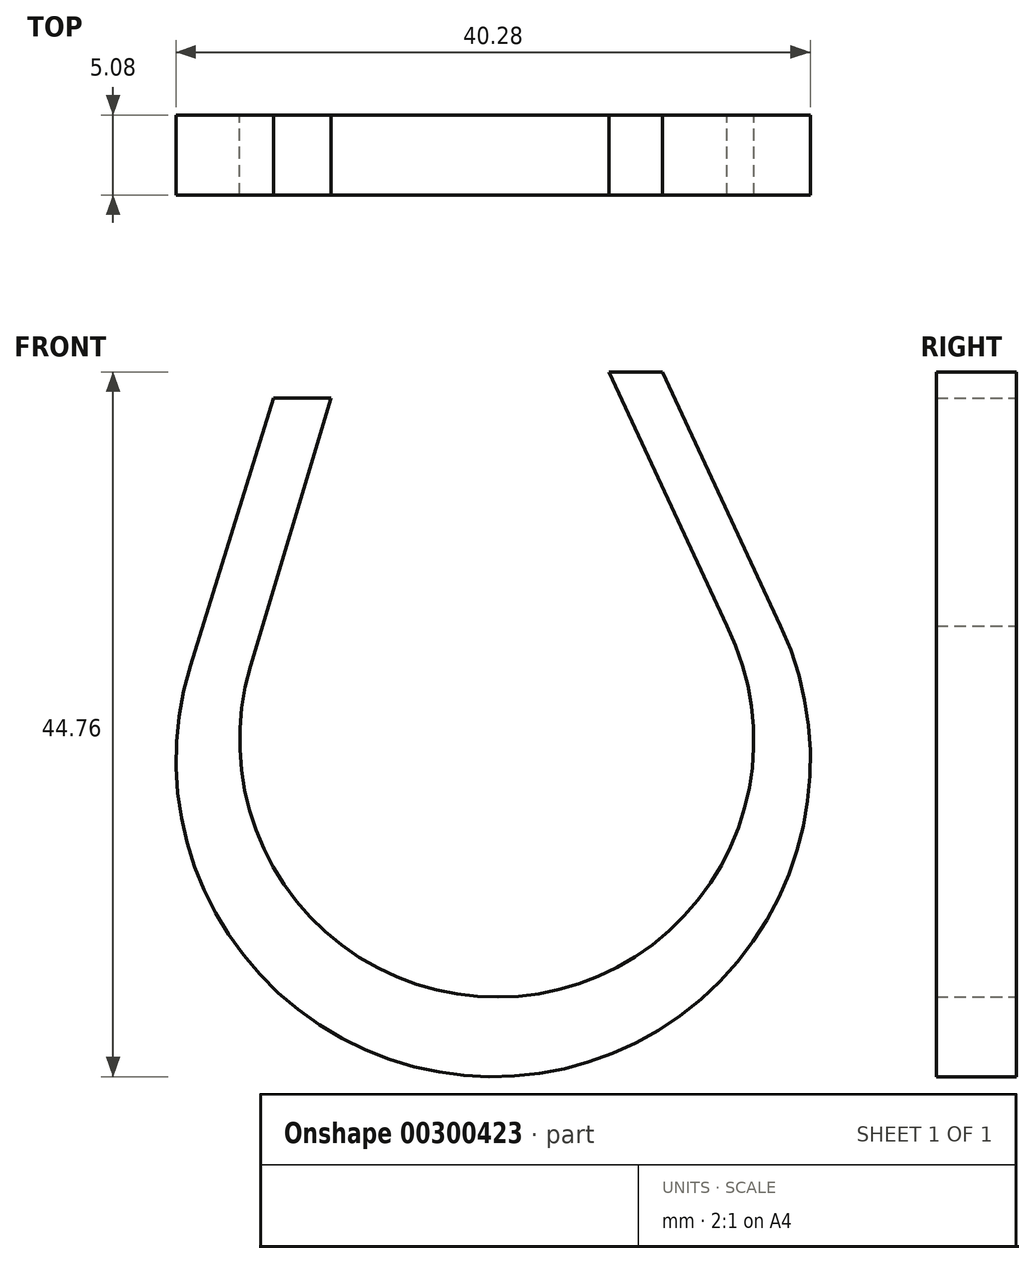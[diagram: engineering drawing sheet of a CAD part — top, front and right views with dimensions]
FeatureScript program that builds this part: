
annotation { "Feature Type Name" : "Feature", "Feature Type Description" : "" }
export const myFeature = defineFeature(function(context is Context, id is Id, definition is map)
    precondition{}
    {
        {
            var Q0;
            Q0=qCreatedBy(makeId("Front.planeOp"),FACE);
            var sketch = newSketch(context, id + "F0", { "sketchPlane" : qUnion([Q0])});
            skArc(sketch, "E0", {"start": v(-30.03, 12.95) * mm, "mid": v(-9.45, -13.14) * mm, "end": v(7.46, 15.46) * mm});
            skLineSegment(sketch, "E1", {"start": v(-30.03, 12.95) * mm, "end": v(-24.74, 29.92) * mm});
            skLineSegment(sketch, "E2", {"start": v(7.46, 15.46) * mm, "end": v(-0.04, 31.58) * mm});
            skLineSegment(sketch, "E3", {"start": v(-21.09, 29.92) * mm, "end": v(-26.2, 12.9) * mm});
            skLineSegment(sketch, "E4", {"start": v(-3.45, 31.58) * mm, "end": v(4.05, 15.46) * mm});
            skArc(sketch, "E5", {"start": v(-26.2, 12.9) * mm, "mid": v(-9.2, -8.07) * mm, "end": v(4.05, 15.46) * mm});
            skLineSegment(sketch, "E6", {"start": v(-21.09, 29.92) * mm, "end": v(-24.74, 29.92) * mm});
            skLineSegment(sketch, "E7", {"start": v(-3.45, 31.58) * mm, "end": v(-0.04, 31.58) * mm});
            skSolve(sketch);
        }
        {
            var Q0;
            Q0=makeQuery(id+"F0.imprint","IMPRINT",FACE,{"disambiguationData":[TD([[makeQuery(id+"F0.imprint","IMPRINT",EDGE,{"derivedFrom":sQuery(id+"F0.wireOp",EDGE,"E0")}),1.0]])]});
            extrude(context, id + "F1", {"entities" : qUnion([Q0]), "depth" : 5.08 * mm});
        }
    });
